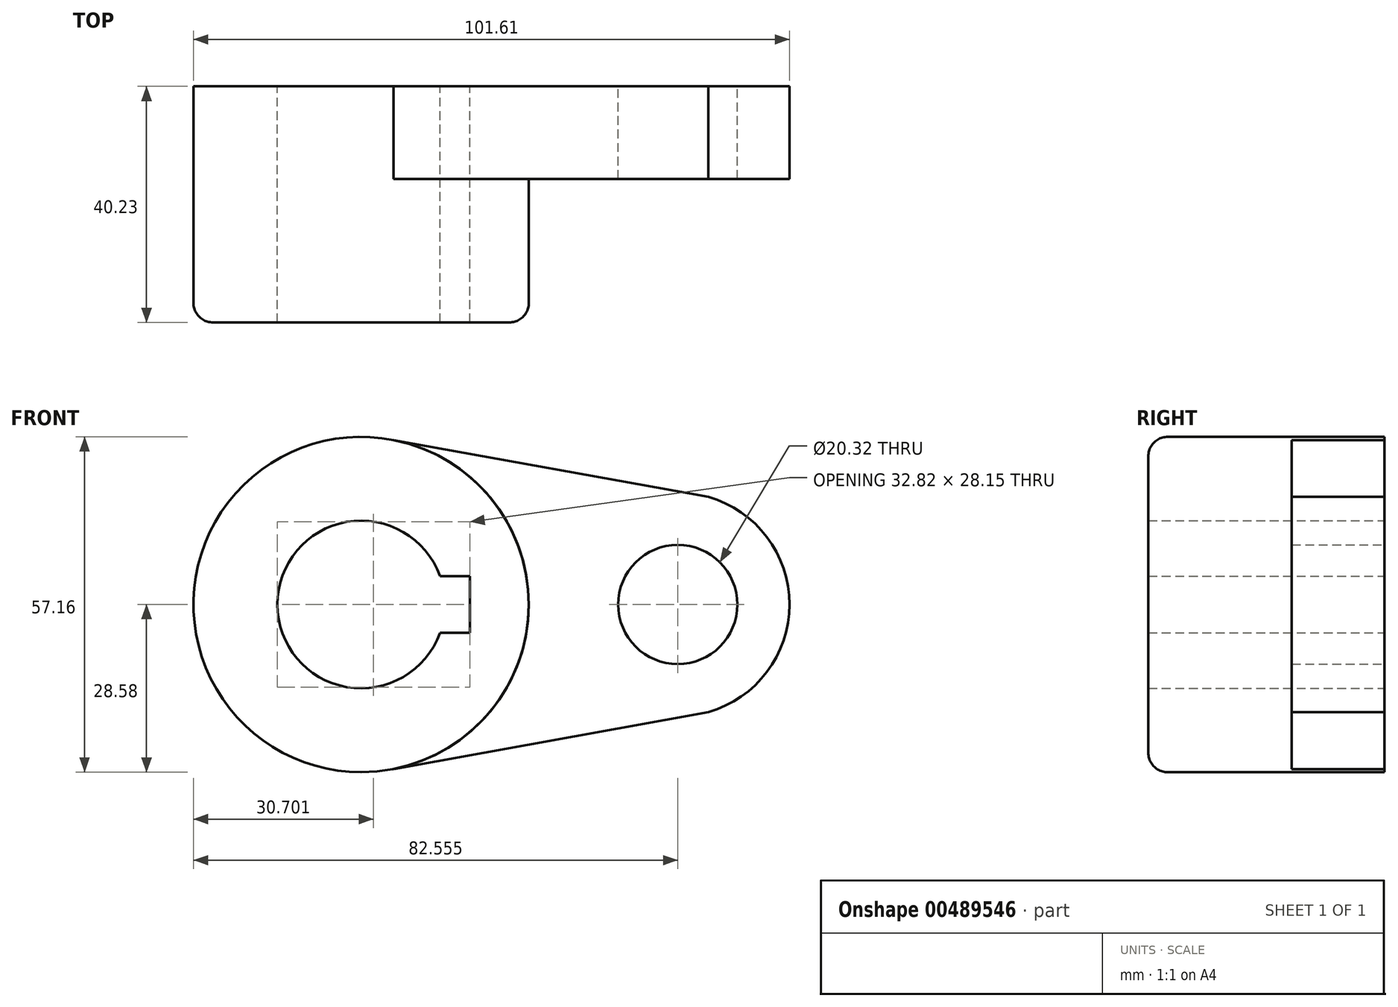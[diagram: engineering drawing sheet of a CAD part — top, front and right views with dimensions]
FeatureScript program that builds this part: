
annotation { "Feature Type Name" : "Feature", "Feature Type Description" : "" }
export const myFeature = defineFeature(function(context is Context, id is Id, definition is map)
    precondition{}
    {
        {
            var Q0;
            Q0=qCreatedBy(makeId("Front.planeOp"),FACE);
            var sketch = newSketch(context, id + "F0", { "sketchPlane" : qUnion([Q0])});
            skArc(sketch, "E0", {"start": v(13.45, 4.83) * mm, "mid": v(-14.29, 0) * mm, "end": v(13.45, -4.83) * mm});
            skCircle(sketch, "E1", {"center": v(0, 0) * mm, "radius": 28.58 * mm});
            skLineSegment(sketch, "E2", {"start": v(0, 0) * mm, "end": v(53.97, 0) * mm, "construction": true});
            skCircle(sketch, "E3", {"center": v(53.97, 0) * mm, "radius": 10.16 * mm});
            skArc(sketch, "E4", {"start": v(73.02, 0) * mm, "mid": v(69.17, 11.49) * mm, "end": v(59.17, 18.33) * mm});
            skLineSegment(sketch, "E5", {"start": v(59.17, 18.33) * mm, "end": v(59.17, -18.33) * mm, "construction": true});
            skArc(sketch, "E6", {"start": v(73.02, 0) * mm, "mid": v(69.17, -11.49) * mm, "end": v(59.17, -18.33) * mm});
            skLineSegment(sketch, "E7", {"start": v(59.17, 18.33) * mm, "end": v(5.54, 28.03) * mm});
            skPoint(sketch, "E8", {"position": v(5.54, -28.03) * mm});
            skLineSegment(sketch, "E9", {"start": v(5.54, -28.03) * mm, "end": v(59.17, -18.33) * mm});
            skLineSegment(sketch, "E10.bottom", {"start": v(18.53, 4.83) * mm, "end": v(13.45, 4.83) * mm});
            skLineSegment(sketch, "E10.top", {"start": v(18.53, -4.83) * mm, "end": v(13.45, -4.83) * mm});
            skLineSegment(sketch, "E10.left", {"start": v(18.53, 4.83) * mm, "end": v(18.53, -4.83) * mm});
            skPoint(sketch, "E10.middle", {"position": v(14.29, 0) * mm});
            skPoint(sketch, "E11.orphan", {"position": v(10.05, 4.83) * mm});
            skPoint(sketch, "E12.orphan", {"position": v(10.05, -4.83) * mm});
            skSolve(sketch);
        }
        {
            var Q0;
            Q0=makeQuery(id+"F0.imprint","IMPRINT",FACE,{"disambiguationData":[TD([[makeQuery(id+"F0.imprint","IMPRINT",EDGE,{"derivedFrom":sQuery(id+"F0.wireOp",EDGE,"E0")}),-1.0]])]});
            extrude(context, id + "F1", {"entities" : qUnion([Q0]), "depth" : 40.23 * mm});
        }
        {
            var Q0;
            Q0=makeQuery(id+"F0.imprint","IMPRINT",FACE,{"disambiguationData":[TD([[makeQuery(id+"F0.imprint","IMPRINT",EDGE,{"derivedFrom":sQuery(id+"F0.wireOp",EDGE,"E3")}),-1.0]])]});
            extrude(context, id + "F2", {"entities" : qUnion([Q0]), "operationType" : NewBodyOperationType.ADD, "depth" : 15.77 * mm});
        }
        {
            var Q0;
            Q0=makeQuery(id+"F1.opExtrude","CAP_EDGE",EDGE,{"disambiguationData":[OSD([sQuery(id+"F0.wireOp",EDGE,"E1")])],"isStart":false});
            fillet(context, id + "F3", {"entities" : qUnion([Q0]), "radius" : 3.3 * mm, "tangentPropagation" : true, "allowEdgeOverflow" : false});
        }
    });
